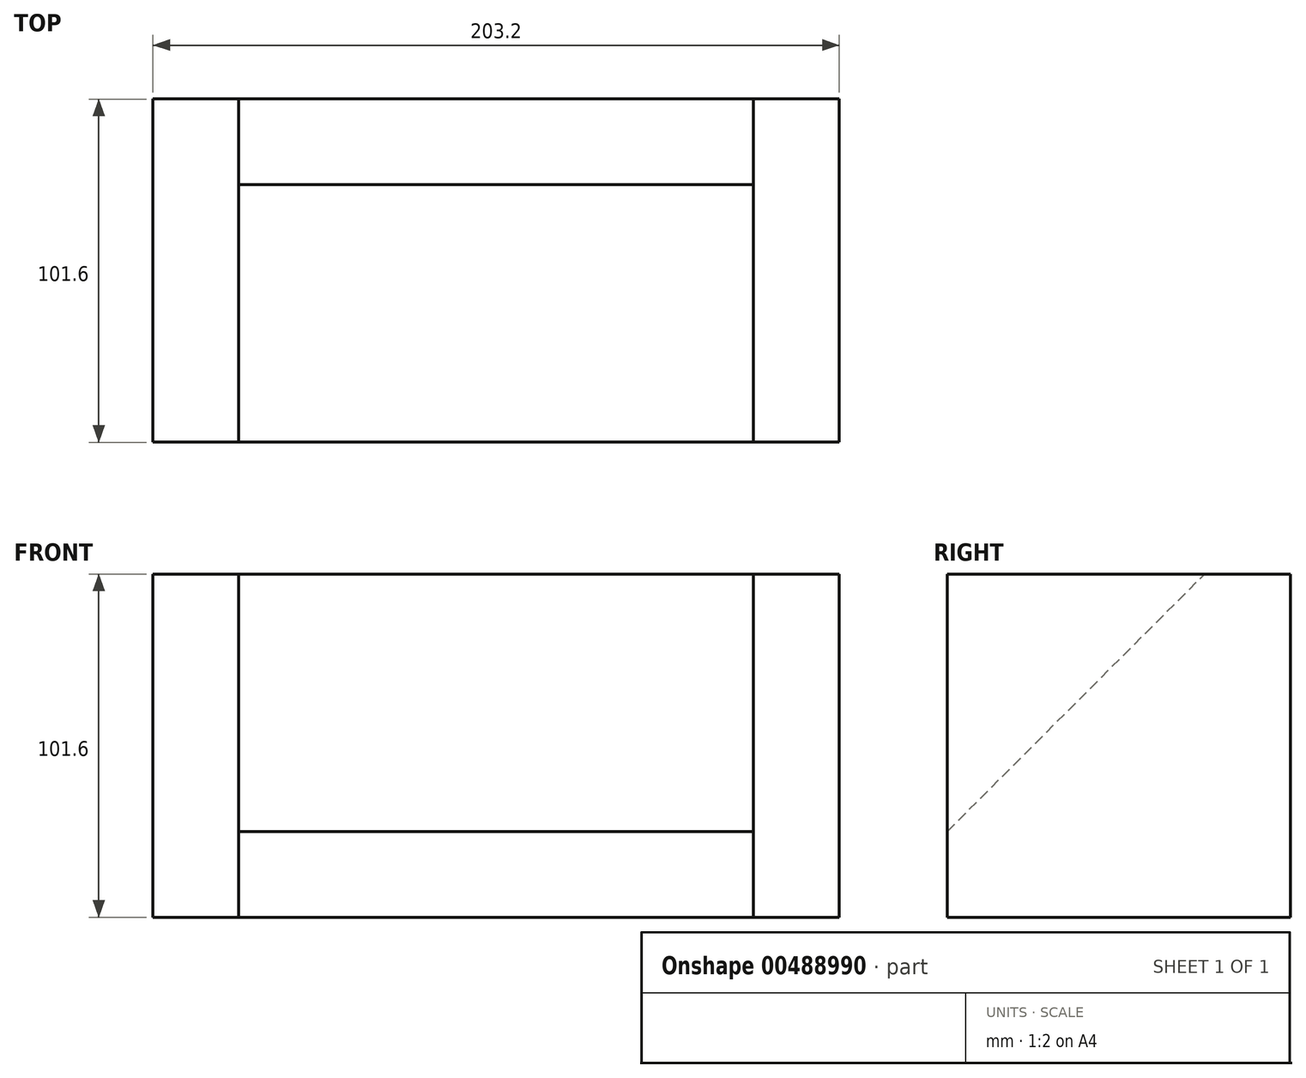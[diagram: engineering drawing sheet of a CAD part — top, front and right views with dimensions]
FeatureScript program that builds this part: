
annotation { "Feature Type Name" : "Feature", "Feature Type Description" : "" }
export const myFeature = defineFeature(function(context is Context, id is Id, definition is map)
    precondition{}
    {
        {
            var Q0;
            Q0=qCreatedBy(makeId("Top.planeOp"),FACE);
            var sketch = newSketch(context, id + "F0", { "sketchPlane" : qUnion([Q0])});
            skLineSegment(sketch, "E0.bottom", {"start": v(-80.14, 69.38) * mm, "end": v(72.26, 69.38) * mm});
            skLineSegment(sketch, "E0.top", {"start": v(-80.14, -32.22) * mm, "end": v(72.26, -32.22) * mm});
            skLineSegment(sketch, "E0.left", {"start": v(-80.14, 69.38) * mm, "end": v(-80.14, -32.22) * mm});
            skLineSegment(sketch, "E0.right", {"start": v(72.26, 69.38) * mm, "end": v(72.26, -32.22) * mm});
            skSolve(sketch);
        }
        {
            var Q0;
            Q0 = qSketchRegion(id + "F0", true);
            extrude(context, id + "F1", {"entities" : qUnion([Q0]), "depth" : 101.6 * mm});
        }
        {
            var Q0;
            Q0=makeQuery(id+"F1.opExtrude","SWEPT_FACE",FACE,{"disambiguationData":[OSD([sQuery(id+"F0.wireOp",EDGE,"E0.right")])]});
            var sketch = newSketch(context, id + "F2", { "sketchPlane" : qUnion([Q0])});
            skLineSegment(sketch, "E1", {"start": v(-32.22, 25.4) * mm, "end": v(43.98, 101.6) * mm});
            skSolve(sketch);
        }
        {
            var Q0;
            {var subQ0=sQuery(id+"F2.wireOp",EDGE,"E1");Q0=makeQuery(id+"F2.imprint","IMPRINT",FACE,{"disambiguationData":[TD([[makeQuery(id+"F2.imprint","IMPRINT",EDGE,{"derivedFrom":subQ0}),1.0]])]});}
            extrude(context, id + "F3", {"entities" : qUnion([Q0]), "operationType" : NewBodyOperationType.REMOVE, "endBound" : BoundingType.THROUGH_ALL, "oppositeDirection" : true, "depth" : 25.4 * mm});
        }
        {
            var Q0;
            Q0=makeQuery(id+"F1.opExtrude","CAP_FACE",FACE,{"disambiguationData":[OSD([sQuery(id+"F0.wireOp",EDGE,"E0.bottom"),sQuery(id+"F0.wireOp",EDGE,"E0.top"),sQuery(id+"F0.wireOp",EDGE,"E0.left"),sQuery(id+"F0.wireOp",EDGE,"E0.right")])],"isStart":false});
            var sketch = newSketch(context, id + "F4", { "sketchPlane" : qUnion([Q0])});
            skLineSegment(sketch, "E2.bottom", {"start": v(-80.14, 69.38) * mm, "end": v(-105.54, 69.38) * mm});
            skLineSegment(sketch, "E2.top", {"start": v(-80.14, -32.22) * mm, "end": v(-105.54, -32.22) * mm});
            skLineSegment(sketch, "E2.left", {"start": v(-80.14, 69.38) * mm, "end": v(-80.14, -32.22) * mm});
            skLineSegment(sketch, "E2.right", {"start": v(-105.54, 69.38) * mm, "end": v(-105.54, -32.22) * mm});
            skLineSegment(sketch, "E3.bottom", {"start": v(72.26, 69.38) * mm, "end": v(97.66, 69.38) * mm});
            skLineSegment(sketch, "E3.top", {"start": v(72.26, -32.22) * mm, "end": v(97.66, -32.22) * mm});
            skLineSegment(sketch, "E3.left", {"start": v(72.26, 69.38) * mm, "end": v(72.26, -32.22) * mm});
            skLineSegment(sketch, "E3.right", {"start": v(97.66, 69.38) * mm, "end": v(97.66, -32.22) * mm});
            skSolve(sketch);
        }
        {
            var Q0;
            Q0 = qSketchRegion(id + "F4", true);
            extrude(context, id + "F5", {"entities" : qUnion([Q0]), "depth" : -101.6 * mm});
        }
    });
